# Revit family: QF_BOURGEAT_CARAVANE_Meubles_buffet_dessus_vitro_chauffant_baie_libre_simple_accès
name_source: partatom
category: Equipement spécialisé
revit_build: Autodesk Revit 2015 (Build: 20140606_1530(x64)
units: mm (PartAtom-declared; Revit-internal decimal feet)

## types (2) — shared parameters
Fabricant = BOURGEAT
Fréquence = 50 Hz
Hauteur hors tout = 1385 mm
Hauteur plan de travail = 839 mm  [stored 2.75262 ft]
Indice de protection = 33
Inox = Acier inoxydable, poli
Phase = 2
Plastique noir = Plastique, noir
Profondeur hors tout = 840 mm
Spécification du Fabricant = Meuble buffet dessus vitro chauffant -baie libre
Tension = 230 V
URL catalogue = http://www.bourgeat.fr
Vitro = Verre vitro

## per-type parameters (varying)
| type | Charge max | Intensité nominale | Longueur de la tablette | Longueur hors tout | Longueur pare-haleine | Modèle | Poids net à vide | Puissance électrique  |
| Modèle simple accès 3 GN | 60.00 kg | 6 A | 1055 mm | 1315 mm  [stored 4.3143 ft] | 1080 mm | 857213 | 180.00 kg | 1310 W |
| Modèle simple accès 4 GN | 80.00 kg | 8 A | 1380 mm  [stored 4.52756 ft] | 1640 mm | 1405 mm  [stored 4.60958 ft] | 857214 | 200.00 kg | 1750 W |

note: [stored X ft] marks values corroborated as IEEE doubles in the binary element streams (Revit-internal decimal feet)

## geometry (parser evidence)
native form markers: Blend x4
no freeform markers — native parametric forms only
